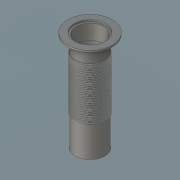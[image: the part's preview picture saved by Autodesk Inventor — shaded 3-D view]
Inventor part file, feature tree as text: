
AUTODESK INVENTOR PART (.ipt)
format: ipt  version: 2018 (Build 220112000, 112)  size: 301,056 bytes
history: native  units: in
note: dims shown in document units (in); Inventor stores cm internally (conversion verified against a paired STEP export)
features: sketch x6, extrude x5, revolve x1
ambient origin geometry x8: Origin, YZ Plane, XZ Plane, XY Plane, X Axis, Y Axis, Z Axis, Center Point
bodies: Solid1 (feature_tree)
feature tree (12):
  extrude  "Extrusion1"  Depth=2.07in
  extrude  "Extrusion2"  Depth=0.12in
  extrude  "Extrusion3"  Depth=0.12in TaperAngle=0.0deg
  extrude  "Extrusion4"  Depth=1.0in TaperAngle=0.0deg
  revolve  "Revolution1"  [1 undecoded]
  extrude  "Extrusion5"  Depth=3.5in
  sketch  "Sketch1"  dims[d0=2.95in d1=2.07in]
  sketch  "Sketch2"  dims[d2=0.12in d3=0.0in d4=0.25in d5=-0.5154in]
  sketch  "Sketch3"  dims[d6=0.12in d7=0.25in d8=0.0in]
  sketch  "Sketch4"  dims[d9=1.97in d10=1.0in d11=0.0in]
  sketch  "Sketch5"  dims[d12=0.05in d15=13.7795in d17=0.1in d18=0.3937in d20=1.0in]
  sketch  "Sketch6"  dims[d22=0.06in d23=3.5in d24=90.0deg d25=2.03in d26=0.0in]
note: 1 required parameter value undecoded (feature->parameter linkage not recoverable at this tier; creation-order binding heuristic only, values carry confidence <= 0.55)
